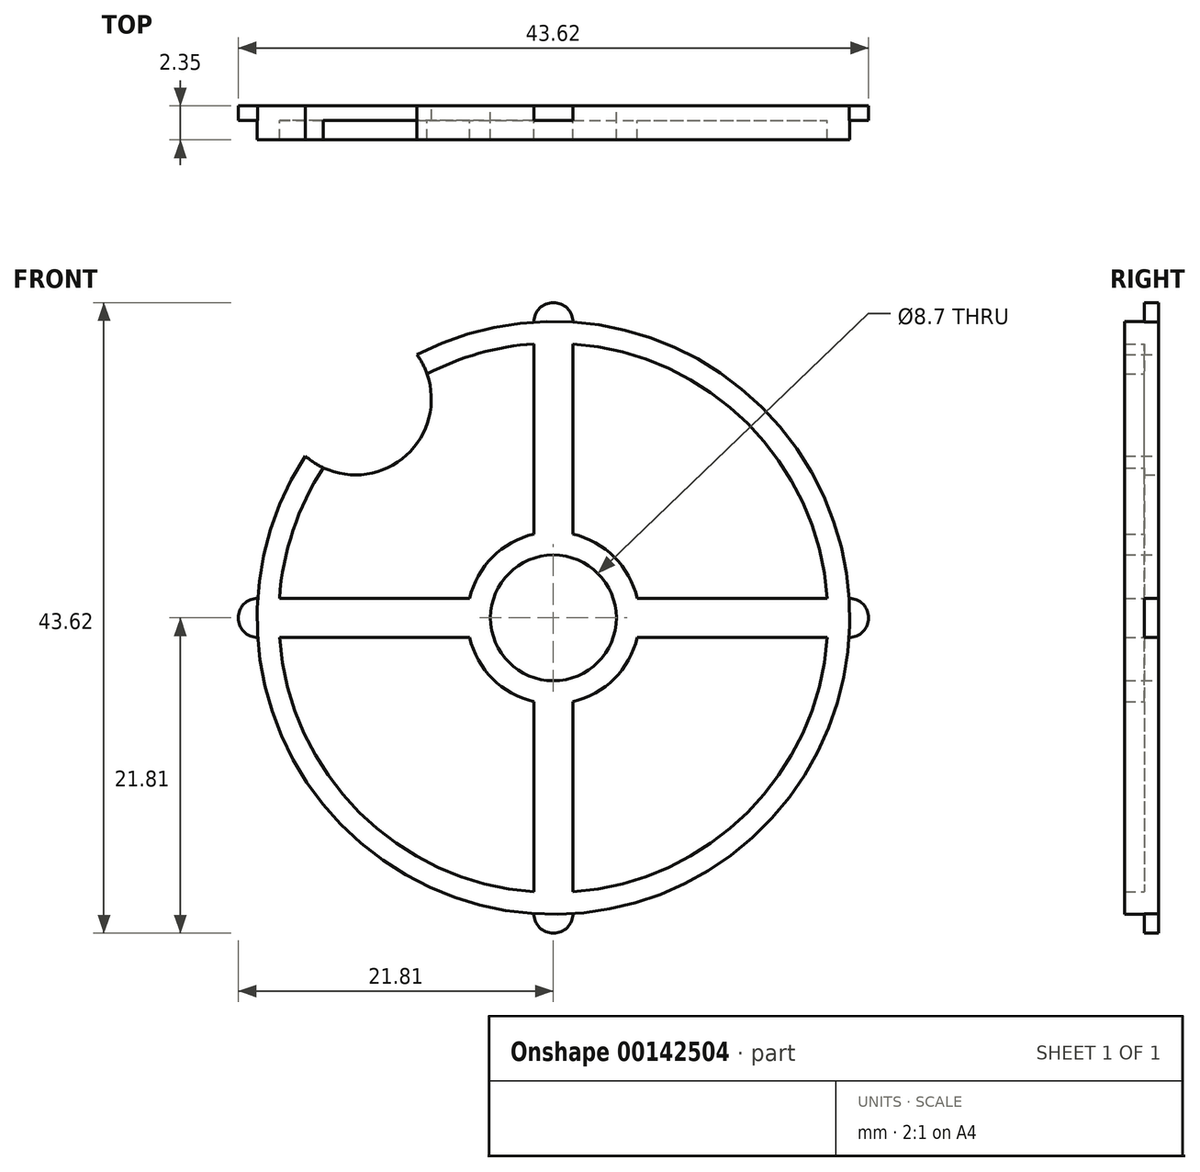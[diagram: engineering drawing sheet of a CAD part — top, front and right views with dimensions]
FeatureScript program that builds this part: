
annotation { "Feature Type Name" : "Feature", "Feature Type Description" : "" }
export const myFeature = defineFeature(function(context is Context, id is Id, definition is map)
    precondition{}
    {
        {
            var Q0;
            Q0=qCreatedBy(makeId("Front.planeOp"),FACE);
            var sketch = newSketch(context, id + "F0", { "sketchPlane" : qUnion([Q0])});
            skCircle(sketch, "E0", {"center": v(0, 0) * mm, "radius": 19 * mm});
            skCircle(sketch, "E1", {"center": v(0, 0) * mm, "radius": 5.95 * mm});
            skLineSegment(sketch, "E2", {"start": v(-1.35, 5.8) * mm, "end": v(-1.35, 18.95) * mm});
            skLineSegment(sketch, "E3", {"start": v(1.35, 5.8) * mm, "end": v(1.35, 18.95) * mm});
            skLineSegment(sketch, "E4", {"start": v(-1.35, -5.8) * mm, "end": v(-1.35, -18.95) * mm});
            skLineSegment(sketch, "E5", {"start": v(1.35, -5.8) * mm, "end": v(1.35, -18.95) * mm});
            skLineSegment(sketch, "E6", {"start": v(-5.8, 1.35) * mm, "end": v(-18.95, 1.35) * mm});
            skLineSegment(sketch, "E7", {"start": v(-5.8, -1.35) * mm, "end": v(-18.95, -1.35) * mm});
            skLineSegment(sketch, "E8", {"start": v(5.8, 1.35) * mm, "end": v(18.95, 1.35) * mm});
            skLineSegment(sketch, "E9", {"start": v(5.8, -1.35) * mm, "end": v(18.95, -1.35) * mm});
            skCircle(sketch, "E10", {"center": v(0, 0) * mm, "radius": 20.5 * mm});
            skCircle(sketch, "E11", {"center": v(0, 0) * mm, "radius": 4.35 * mm});
            skArc(sketch, "E12", {"start": v(-17.17, 11.2) * mm, "mid": v(-10.17, 11.24) * mm, "end": v(-9.43, 18.2) * mm});
            skLineSegment(sketch, "E13", {"start": v(-1.35, 18.95) * mm, "end": v(-1.35, 20.46) * mm, "construction": true});
            skLineSegment(sketch, "E14", {"start": v(1.35, 18.95) * mm, "end": v(1.35, 20.46) * mm, "construction": true});
            skArc(sketch, "E15", {"start": v(1.35, 20.46) * mm, "mid": v(0, 21.8) * mm, "end": v(-1.35, 20.46) * mm});
            skLineSegment(sketch, "E16", {"start": v(-18.95, 1.35) * mm, "end": v(-20.46, 1.35) * mm, "construction": true});
            skLineSegment(sketch, "E17", {"start": v(-18.95, -1.35) * mm, "end": v(-20.46, -1.35) * mm, "construction": true});
            skArc(sketch, "E18", {"start": v(-20.46, 1.35) * mm, "mid": v(-21.8, 0) * mm, "end": v(-20.46, -1.35) * mm});
            skLineSegment(sketch, "E19", {"start": v(-1.35, -18.95) * mm, "end": v(-1.35, -20.46) * mm, "construction": true});
            skLineSegment(sketch, "E20", {"start": v(1.35, -18.95) * mm, "end": v(1.35, -20.46) * mm, "construction": true});
            skArc(sketch, "E21", {"start": v(-1.35, -20.46) * mm, "mid": v(0, -21.8) * mm, "end": v(1.35, -20.46) * mm});
            skLineSegment(sketch, "E22", {"start": v(18.95, 1.35) * mm, "end": v(20.46, 1.35) * mm, "construction": true});
            skLineSegment(sketch, "E23", {"start": v(18.95, -1.35) * mm, "end": v(20.46, -1.35) * mm, "construction": true});
            skArc(sketch, "E24", {"start": v(20.46, -1.35) * mm, "mid": v(21.8, 0) * mm, "end": v(20.46, 1.35) * mm});
            skSolve(sketch);
        }
        {
            var Q0;
            {var subQ4=sQuery(id+"F0.wireOp",EDGE,"E0");var subQ7=makeQuery(id+"F0.imprint","INTERSECT",VERTEX,{"derivedFrom":[subQ4,sQuery(id+"F0.wireOp",EDGE,"E3")]});Q0=makeQuery(id+"F0.imprint","IMPRINT",FACE,{"disambiguationData":[TD([[makeQuery(id+"F0.imprint","IMPRINT",EDGE,{"disambiguationData":[TD([[subQ7,1.0]])],"derivedFrom":subQ4}),-1.0]])]});}
            var Q1;
            {var subQ0=sQuery(id+"F0.wireOp",EDGE,"E4");Q1=makeQuery(id+"F0.imprint","IMPRINT",FACE,{"disambiguationData":[TD([[makeQuery(id+"F0.imprint","IMPRINT",EDGE,{"derivedFrom":subQ0}),1.0]])]});}
            var Q2;
            {var subQ0=sQuery(id+"F0.wireOp",EDGE,"E8");Q2=makeQuery(id+"F0.imprint","IMPRINT",FACE,{"disambiguationData":[TD([[makeQuery(id+"F0.imprint","IMPRINT",EDGE,{"derivedFrom":subQ0}),-1.0]])]});}
            var Q3;
            {var subQ0=sQuery(id+"F0.wireOp",EDGE,"E6");Q3=makeQuery(id+"F0.imprint","IMPRINT",FACE,{"disambiguationData":[TD([[makeQuery(id+"F0.imprint","IMPRINT",EDGE,{"derivedFrom":subQ0}),1.0]])]});}
            var Q4;
            {var subQ0=sQuery(id+"F0.wireOp",EDGE,"E2");Q4=makeQuery(id+"F0.imprint","IMPRINT",FACE,{"disambiguationData":[TD([[makeQuery(id+"F0.imprint","IMPRINT",EDGE,{"derivedFrom":subQ0}),-1.0]])]});}
            var Q5;
            {var subQ0=sQuery(id+"F0.wireOp",EDGE,"JQplNzLy-MDn4-o3jD-dyHa-r76O8bGRBZya");Q5=makeQuery(id+"F0.imprint","IMPRINT",FACE,{"disambiguationData":[TD([[makeQuery(id+"F0.imprint","IMPRINT",EDGE,{"derivedFrom":subQ0}),1.0]])]});}
            var Q6;
            {var subQ0=sQuery(id+"F0.wireOp",EDGE,"iP1EGVPw-j7wL-WCFN-5Kgd-LL717Ze5B378");Q6=makeQuery(id+"F0.imprint","IMPRINT",FACE,{"disambiguationData":[TD([[makeQuery(id+"F0.imprint","IMPRINT",EDGE,{"derivedFrom":subQ0}),1.0]])]});}
            var Q7;
            {var subQ0=sQuery(id+"F0.wireOp",EDGE,"CEaXaM09-qpk9-WgmC-VFXw-WiOaJCkjnFe9");Q7=makeQuery(id+"F0.imprint","IMPRINT",FACE,{"disambiguationData":[TD([[makeQuery(id+"F0.imprint","IMPRINT",EDGE,{"derivedFrom":subQ0}),1.0]])]});}
            var Q8;
            {var subQ0=sQuery(id+"F0.wireOp",EDGE,"5ZXZNUGm-eNXA-uQi5-Vss4-XkvxrCQkCZnC");Q8=makeQuery(id+"F0.imprint","IMPRINT",FACE,{"disambiguationData":[TD([[makeQuery(id+"F0.imprint","IMPRINT",EDGE,{"derivedFrom":subQ0}),1.0]])]});}
            var Q9;
            {var subQ0=sQuery(id+"F0.wireOp",EDGE,"E1");var subQ4=makeQuery(id+"F0.imprint","INTERSECT",VERTEX,{"derivedFrom":[subQ0,sQuery(id+"F0.wireOp",EDGE,"E3")]});Q9=makeQuery(id+"F0.imprint","IMPRINT",FACE,{"disambiguationData":[TD([[makeQuery(id+"F0.imprint","IMPRINT",EDGE,{"disambiguationData":[TD([[subQ4,1.0]])],"derivedFrom":subQ0}),1.0]])]});}
            extrude(context, id + "F1", {"entities" : qUnion([Q0, Q1, Q2, Q3, Q4, Q5, Q6, Q7, Q8, Q9]), "depth" : 2.35 * mm});
        }
        {
            var Q0;
            {var subQ0=sQuery(id+"F0.wireOp",EDGE,"E2");Q0=makeQuery(id+"F0.imprint","IMPRINT",FACE,{"disambiguationData":[TD([[makeQuery(id+"F0.imprint","IMPRINT",EDGE,{"derivedFrom":subQ0}),1.0]])]});}
            var Q1;
            {var subQ0=sQuery(id+"F0.wireOp",EDGE,"E5");Q1=makeQuery(id+"F0.imprint","IMPRINT",FACE,{"disambiguationData":[TD([[makeQuery(id+"F0.imprint","IMPRINT",EDGE,{"derivedFrom":subQ0}),1.0]])]});}
            var Q2;
            {var subQ0=sQuery(id+"F0.wireOp",EDGE,"E3");Q2=makeQuery(id+"F0.imprint","IMPRINT",FACE,{"disambiguationData":[TD([[makeQuery(id+"F0.imprint","IMPRINT",EDGE,{"derivedFrom":subQ0}),-1.0]])]});}
            var Q3;
            {var subQ0=sQuery(id+"F0.wireOp",EDGE,"E4");Q3=makeQuery(id+"F0.imprint","IMPRINT",FACE,{"disambiguationData":[TD([[makeQuery(id+"F0.imprint","IMPRINT",EDGE,{"derivedFrom":subQ0}),-1.0]])]});}
            var Q4;
            {var subQ0=sQuery(id+"F0.wireOp",EDGE,"E18");Q4=makeQuery(id+"F0.imprint","IMPRINT",FACE,{"disambiguationData":[TD([[makeQuery(id+"F0.imprint","IMPRINT",EDGE,{"derivedFrom":subQ0}),1.0]])]});}
            var Q5;
            {var subQ0=sQuery(id+"F0.wireOp",EDGE,"E21");Q5=makeQuery(id+"F0.imprint","IMPRINT",FACE,{"disambiguationData":[TD([[makeQuery(id+"F0.imprint","IMPRINT",EDGE,{"derivedFrom":subQ0}),1.0]])]});}
            var Q6;
            {var subQ0=sQuery(id+"F0.wireOp",EDGE,"E24");Q6=makeQuery(id+"F0.imprint","IMPRINT",FACE,{"disambiguationData":[TD([[makeQuery(id+"F0.imprint","IMPRINT",EDGE,{"derivedFrom":subQ0}),1.0]])]});}
            var Q7;
            {var subQ0=sQuery(id+"F0.wireOp",EDGE,"E15");Q7=makeQuery(id+"F0.imprint","IMPRINT",FACE,{"disambiguationData":[TD([[makeQuery(id+"F0.imprint","IMPRINT",EDGE,{"derivedFrom":subQ0}),1.0]])]});}
            extrude(context, id + "F2", {"entities" : qUnion([Q0, Q1, Q2, Q3, Q4, Q5, Q6, Q7]), "operationType" : NewBodyOperationType.ADD, "depth" : 1 * mm});
        }
        {
            var Q0;
            Q0=qSketchRegion(id+"F0",true);
            extrude(context, id + "F3", {"entities" : qUnion([Q0]), "operationType" : NewBodyOperationType.REMOVE, "oppositeDirection" : true, "depth" : 25 * mm});
        }
    });
